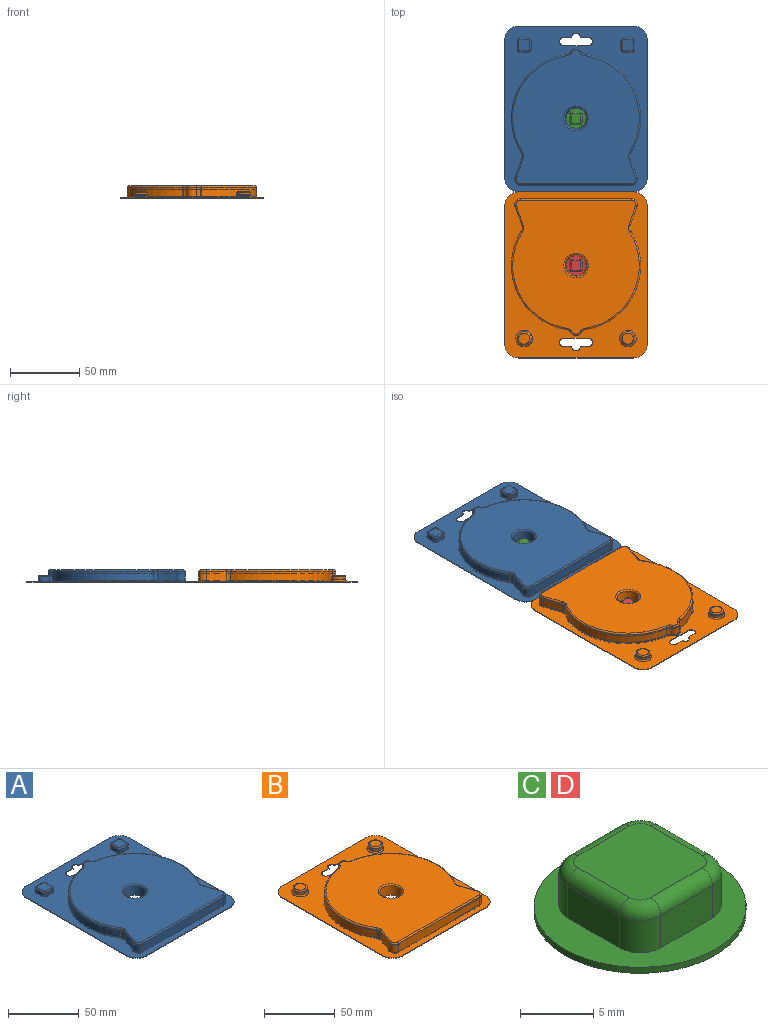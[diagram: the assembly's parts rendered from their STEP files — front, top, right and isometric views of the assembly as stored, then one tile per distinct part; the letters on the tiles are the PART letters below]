
ASSEMBLY  parts=4 mates=6
PART A: 168 faces, bbox 104.4x120x8.7 mm
  f0: plane 120x103mm, normal (0,0,-1), area 4033mm2, adj f3,f4,f5,f6,f7,f8,f9,f10
  f1: plane 15x15mm, normal (0,0,-1), area 12.1mm2, adj f48,f117
  f2: plane 120x103mm, normal (0,0,1), area 4313.1mm2, adj f3,f4,f5,f6,f7,f8,f9,f10
  f3: plane 100x0.5mm, normal (1,0,0), area 50mm2, adj f0,f2,f4,f16
  f4: cylinder r=10mm len=10mm, axis (0,0,-1), area 7.9mm2, adj f0,f2,f3,f5
  f5: plane 83x0.5mm, normal (0,1,0), area 41.5mm2, adj f0,f2,f4,f6
  f6: cylinder r=10mm len=10mm, axis (0,0,-1), area 7.9mm2, adj f0,f2,f5,f7
  f7: plane 100x0.5mm, normal (-1,0,0), area 50mm2, adj f0,f2,f6,f8
  f8: cylinder r=10mm len=10mm, axis (0,0,-1), area 7.9mm2, adj f0,f2,f7,f9
  f9: plane 83x0.5mm, normal (0,-1,0), area 41.5mm2, adj f0,f2,f8,f16
  f10: plane 18x0.5mm, normal (0,1,0), area 9mm2, adj f0,f2,f11,f15
  f11: cylinder r=3mm len=6mm, axis (0,0,-1), area 4.7mm2, adj f0,f2,f10,f12
  f12: plane 6x0.5mm, normal (0,-1,0), area 3mm2, adj f0,f2,f11,f13
  f13: cylinder r=3mm len=6mm, axis (0,0,-1), area 4.7mm2, adj f0,f2,f12,f14
  f14: plane 6x0.5mm, normal (0,-1,0), area 3mm2, adj f0,f2,f13,f15
  f15: cylinder r=3mm len=6mm, axis (0,0,-1), area 4.7mm2, adj f0,f2,f10,f14
  f16: cylinder r=10mm len=10mm, axis (0,0,-1), area 7.9mm2, adj f0,f2,f3,f9
  f17: cylinder r=4mm len=7.2mm, axis (0,0,-1), area 26.2mm2, adj f2,f18,f28,f58
  f18: plane 14.27x7.2mm, normal (-0.94,0.34,0), area 109mm2, adj f2,f17,f19,f60
  f19: cylinder r=4mm len=7.2mm, axis (0,0,-1), area 55.1mm2, adj f2,f18,f20,f59
  f20: plane 80.66x7.2mm, normal (0,-1,0), area 580.7mm2, adj f2,f19,f21,f57
  f21: cylinder r=4mm len=7.2mm, axis (0,0,-1), area 55.1mm2, adj f2,f20,f22,f55
  f22: plane 14.27x7.2mm, normal (0.94,0.34,0), area 109mm2, adj f2,f21,f23,f53
  f23: cylinder r=4mm len=7.2mm, axis (0,0,-1), area 26.2mm2, adj f2,f22,f24,f51
  f24: cylinder r=46.75mm len=71.42mm, axis (0,0,-1), area 672mm2, adj f2,f23,f25,f49
  f25: cylinder r=4mm len=7.2mm, axis (0,0,-1), area 28.2mm2, adj f2,f24,f26,f50
  f26: cylinder r=4mm len=7.2mm, axis (0,0,-1), area 64.5mm2, adj f2,f25,f27,f52
  f27: cylinder r=4mm len=7.2mm, axis (0,0,-1), area 28.2mm2, adj f2,f26,f28,f54
  f28: cylinder r=46.75mm len=71.42mm, axis (0,0,-1), area 672mm2, adj f2,f17,f27,f56
  f29: plane 97x91.5mm, normal (0,0,1), area 7034mm2, adj f49,f50,f51,f52,f53,f54,f55,f56
  f30: plane 6x3.2mm, normal (-1,0,0), area 19.2mm2, adj f2,f31,f37,f75
  f31: cylinder r=2mm len=3.2mm, axis (0,0,-1), area 10.1mm2, adj f2,f30,f32,f77
  f32: plane 6x3.2mm, normal (0,-1,0), area 19.2mm2, adj f2,f31,f33,f76
  f33: cylinder r=2mm len=3.2mm, axis (0,0,-1), area 10.1mm2, adj f2,f32,f34,f74
  f34: plane 6x3.2mm, normal (1,0,0), area 19.2mm2, adj f2,f33,f35,f72
  f35: cylinder r=2mm len=3.2mm, axis (0,0,-1), area 10.1mm2, adj f2,f34,f36,f70
  f36: plane 6x3.2mm, normal (0,1,0), area 19.2mm2, adj f2,f35,f37,f71
  f37: cylinder r=2mm len=3.2mm, axis (0,0,-1), area 10.1mm2, adj f2,f30,f36,f73
  f38: plane 8x8mm, normal (0,0,1), area 63.1mm2, adj f70,f71,f72,f73,f74,f75,f76,f77
  f39: plane 6x3.2mm, normal (1,0,0), area 19.2mm2, adj f2,f40,f46,f66
  f40: cylinder r=2mm len=3.2mm, axis (0,0,-1), area 10.1mm2, adj f2,f39,f41,f64
  f41: plane 6x3.2mm, normal (0,1,0), area 19.2mm2, adj f2,f40,f42,f62
  f42: cylinder r=2mm len=3.2mm, axis (0,0,-1), area 10.1mm2, adj f2,f41,f43,f63
  f43: plane 6x3.2mm, normal (-1,0,0), area 19.2mm2, adj f2,f42,f44,f65
  f44: cylinder r=2mm len=3.2mm, axis (0,0,-1), area 10.1mm2, adj f2,f43,f45,f67
  f45: plane 6x3.2mm, normal (0,-1,0), area 19.2mm2, adj f2,f44,f46,f69
  f46: cylinder r=2mm len=3.2mm, axis (0,0,-1), area 10.1mm2, adj f2,f39,f45,f68
  f47: plane 8x8mm, normal (0,0,1), area 63.1mm2, adj f62,f63,f64,f65,f66,f67,f68,f69
  f48: cone r=8mm half-angle=5deg, axis (0,0,1), area 372.3mm2, adj f1,f61
  f49: torus R=45.75mm, axis (0,0,1), area 145.5mm2, adj f24,f29,f50,f51
  f50: torus R=5mm, axis (0,0,1), area 6.7mm2, adj f25,f29,f49,f52
  f51: torus R=5mm, axis (0,0,1), area 6.2mm2, adj f23,f29,f49,f53
  f52: torus R=3mm, axis (0,0,1), area 12.8mm2, adj f26,f29,f50,f54
  f53: cylinder r=1mm len=14.6mm, axis (0.34,-0.94,0), area 23.8mm2, adj f22,f29,f51,f55
  f54: torus R=5mm, axis (0,0,1), area 6.7mm2, adj f27,f29,f52,f56
  f55: torus R=3mm, axis (0,0,1), area 10.9mm2, adj f21,f29,f53,f57
  f56: torus R=45.75mm, axis (0,0,1), area 145.5mm2, adj f28,f29,f54,f58
  f57: cylinder r=1mm len=80.66mm, axis (-1,0,0), area 126.7mm2, adj f20,f29,f55,f59
  f58: torus R=5mm, axis (0,0,1), area 6.2mm2, adj f17,f29,f56,f60
  f59: torus R=3mm, axis (0,0,1), area 10.9mm2, adj f19,f29,f57,f60
  f60: cylinder r=1mm len=14.6mm, axis (0.34,0.94,0), area 23.8mm2, adj f18,f29,f58,f59
  f61: torus R=8.92mm, axis (0,0,1), area 77.4mm2, adj f29,f48
  f62: cylinder r=1mm len=6mm, axis (1,0,0), area 9.4mm2, adj f41,f47,f63,f64
  f63: torus R=1mm, axis (0,0,1), area 4mm2, adj f42,f47,f62,f65
  f64: torus R=1mm, axis (0,0,1), area 4mm2, adj f40,f47,f62,f66
  f65: cylinder r=1mm len=6mm, axis (0,1,0), area 9.4mm2, adj f43,f47,f63,f67
  f66: cylinder r=1mm len=6mm, axis (0,-1,0), area 9.4mm2, adj f39,f47,f64,f68
  f67: torus R=1mm, axis (0,0,1), area 4mm2, adj f44,f47,f65,f69
  f68: torus R=1mm, axis (0,0,1), area 4mm2, adj f46,f47,f66,f69
  f69: cylinder r=1mm len=6mm, axis (-1,0,0), area 9.4mm2, adj f45,f47,f67,f68
  f70: torus R=1mm, axis (0,0,1), area 4mm2, adj f35,f38,f71,f72
  f71: cylinder r=1mm len=6mm, axis (1,0,0), area 9.4mm2, adj f36,f38,f70,f73
  f72: cylinder r=1mm len=6mm, axis (0,-1,0), area 9.4mm2, adj f34,f38,f70,f74
  f73: torus R=1mm, axis (0,0,1), area 4mm2, adj f37,f38,f71,f75
  f74: torus R=1mm, axis (0,0,1), area 4mm2, adj f33,f38,f72,f76
  f75: cylinder r=1mm len=6mm, axis (0,1,0), area 9.4mm2, adj f30,f38,f73,f77
  f76: cylinder r=1mm len=6mm, axis (-1,0,0), area 9.4mm2, adj f32,f38,f74,f77
  f77: torus R=1mm, axis (0,0,1), area 4mm2, adj f31,f38,f75,f76
  f78: cylinder r=4mm len=5.5mm, axis (0,0,-1), area 20.6mm2, adj f79,f89,f93,f114
  f79: plane 13.64x5.5mm, normal (-0.94,-0.35,0), area 80.2mm2, adj f78,f80,f95,f112
  f80: cylinder r=4mm len=5.5mm, axis (0,0,-1), area 42.5mm2, adj f79,f81,f97,f110
  f81: plane 80x5.5mm, normal (0,1,0), area 440mm2, adj f80,f82,f99,f108
  f82: cylinder r=4mm len=5.5mm, axis (0,0,-1), area 42.5mm2, adj f81,f83,f101,f106
  f83: plane 13.64x5.5mm, normal (0.94,-0.35,0), area 80.2mm2, adj f82,f84,f103,f104
  f84: cylinder r=4mm len=5.5mm, axis (0,0,-1), area 20.6mm2, adj f83,f85,f102,f105
  f85: cylinder r=46.5mm len=71.39mm, axis (0,0,-1), area 513.3mm2, adj f84,f86,f100,f107
  f86: cylinder r=4mm len=5.5mm, axis (0,0,-1), area 20.7mm2, adj f85,f87,f98,f109
  f87: cylinder r=4mm len=7.07mm, axis (0,0,-1), area 47.6mm2, adj f86,f88,f96,f111
  f88: cylinder r=4mm len=5.5mm, axis (0,0,-1), area 20.7mm2, adj f87,f89,f94,f113
  f89: cylinder r=46.5mm len=71.39mm, axis (0,0,-1), area 513.3mm2, adj f78,f88,f92,f115
  f90: cylinder r=8.5mm len=17mm, axis (0,0,-1), area 293.7mm2, adj f116,f117
  f91: plane 96.25x91mm, normal (0,0,-1), area 6910.7mm2, adj f104,f105,f106,f107,f108,f109,f110,f111
  f92: torus R=47.5mm, axis (0,0,1), area 147.7mm2, adj f0,f89,f93,f94
  f93: torus R=3mm, axis (0,0,1), area 5.4mm2, adj f0,f78,f92,f95
  f94: torus R=3mm, axis (0,0,1), area 5.4mm2, adj f0,f88,f92,f96
  f95: cylinder r=1mm len=14mm, axis (0.35,-0.94,0), area 22.9mm2, adj f0,f79,f93,f97
  f96: torus R=5mm, axis (0,0,1), area 14.8mm2, adj f0,f87,f94,f98
  f97: torus R=5mm, axis (0,0,1), area 13.2mm2, adj f0,f80,f95,f99
  f98: torus R=3mm, axis (0,0,1), area 5.4mm2, adj f0,f86,f96,f100
  f99: cylinder r=1mm len=80mm, axis (-1,0,0), area 125.7mm2, adj f0,f81,f97,f101
  f100: torus R=47.5mm, axis (0,0,1), area 147.7mm2, adj f0,f85,f98,f102
  f101: torus R=5mm, axis (0,0,1), area 13.2mm2, adj f0,f82,f99,f103
  f102: torus R=3mm, axis (0,0,1), area 5.4mm2, adj f0,f84,f100,f103
  f103: cylinder r=1mm len=14mm, axis (0.35,0.94,0), area 22.9mm2, adj f0,f83,f101,f102
  f104: cylinder r=1mm len=14mm, axis (0.35,0.94,0), area 22.9mm2, adj f83,f91,f105,f106
  f105: torus R=5mm, axis (0,0,-1), area 6.4mm2, adj f84,f91,f104,f107
  f106: torus R=3mm, axis (0,0,-1), area 11mm2, adj f82,f91,f104,f108
  f107: torus R=45.5mm, axis (0,0,-1), area 145.5mm2, adj f85,f91,f105,f109
  f108: cylinder r=1mm len=80mm, axis (-1,0,0), area 125.7mm2, adj f81,f91,f106,f110
  f109: torus R=5mm, axis (0,0,-1), area 6.5mm2, adj f86,f91,f107,f111
  f110: torus R=3mm, axis (0,0,-1), area 11mm2, adj f80,f91,f108,f112
  f111: torus R=3mm, axis (0,0,-1), area 12.4mm2, adj f87,f91,f109,f113
  f112: cylinder r=1mm len=14mm, axis (0.35,-0.94,0), area 22.9mm2, adj f79,f91,f110,f114
  f113: torus R=5mm, axis (0,0,-1), area 6.5mm2, adj f88,f91,f111,f115
  f114: torus R=5mm, axis (0,0,-1), area 6.4mm2, adj f78,f91,f112,f115
  f115: torus R=45.5mm, axis (0,0,-1), area 145.5mm2, adj f89,f91,f113,f114
  f116: torus R=9.5mm, axis (0,0,-1), area 87.5mm2, adj f90,f91
  f117: torus R=7.5mm, axis (0,0,1), area 80.3mm2, adj f1,f90
  f118: plane 5x1.7mm, normal (-1,0,0), area 8.5mm2, adj f119,f125,f143,f156
  f119: cylinder r=2mm len=2mm, axis (0,0,-1), area 5.3mm2, adj f118,f120,f141,f154
  f120: plane 5x1.7mm, normal (0,1,0), area 8.5mm2, adj f119,f121,f139,f152
  f121: cylinder r=2mm len=2mm, axis (0,0,-1), area 5.3mm2, adj f120,f122,f137,f153
  f122: plane 5x1.7mm, normal (1,0,0), area 8.5mm2, adj f121,f123,f136,f155
  f123: cylinder r=2mm len=2mm, axis (0,0,-1), area 5.3mm2, adj f122,f124,f138,f157
  f124: plane 5x1.7mm, normal (0,-1,0), area 8.5mm2, adj f123,f125,f140,f159
  f125: cylinder r=2mm len=2mm, axis (0,0,-1), area 5.3mm2, adj f118,f124,f142,f158
  f126: plane 7x7mm, normal (0,0,-1), area 48.1mm2, adj f152,f153,f154,f155,f156,f157,f158,f159
  f127: plane 5x1.7mm, normal (1,0,0), area 8.5mm2, adj f128,f134,f144,f165
  f128: cylinder r=2mm len=2mm, axis (0,0,-1), area 5.3mm2, adj f127,f129,f146,f167
  f129: plane 5x1.7mm, normal (0,-1,0), area 8.5mm2, adj f128,f130,f148,f166
  f130: cylinder r=2mm len=2mm, axis (0,0,-1), area 5.3mm2, adj f129,f131,f150,f164
  f131: plane 5x1.7mm, normal (-1,0,0), area 8.5mm2, adj f130,f132,f151,f162
  f132: cylinder r=2mm len=2mm, axis (0,0,-1), area 5.3mm2, adj f131,f133,f149,f160
  f133: plane 5x1.7mm, normal (0,1,0), area 8.5mm2, adj f132,f134,f147,f161
  f134: cylinder r=2mm len=2mm, axis (0,0,-1), area 5.3mm2, adj f127,f133,f145,f163
  f135: plane 7x7mm, normal (0,0,-1), area 48.1mm2, adj f160,f161,f162,f163,f164,f165,f166,f167
  f136: cylinder r=1mm len=5mm, axis (0,1,0), area 7.9mm2, adj f0,f122,f137,f138
  f137: torus R=3mm, axis (0,0,1), area 5.8mm2, adj f0,f121,f136,f139
  f138: torus R=3mm, axis (0,0,1), area 5.8mm2, adj f0,f123,f136,f140
  f139: cylinder r=1mm len=5mm, axis (-1,0,0), area 7.9mm2, adj f0,f120,f137,f141
  f140: cylinder r=1mm len=5mm, axis (1,0,0), area 7.9mm2, adj f0,f124,f138,f142
  f141: torus R=3mm, axis (0,0,1), area 5.8mm2, adj f0,f119,f139,f143
  f142: torus R=3mm, axis (0,0,1), area 5.8mm2, adj f0,f125,f140,f143
  f143: cylinder r=1mm len=5mm, axis (0,-1,0), area 7.9mm2, adj f0,f118,f141,f142
  f144: cylinder r=1mm len=5mm, axis (0,1,0), area 7.9mm2, adj f0,f127,f145,f146
  f145: torus R=3mm, axis (0,0,1), area 5.8mm2, adj f0,f134,f144,f147
  f146: torus R=3mm, axis (0,0,1), area 5.8mm2, adj f0,f128,f144,f148
  f147: cylinder r=1mm len=5mm, axis (-1,0,0), area 7.9mm2, adj f0,f133,f145,f149
  f148: cylinder r=1mm len=5mm, axis (1,0,0), area 7.9mm2, adj f0,f129,f146,f150
  f149: torus R=3mm, axis (0,0,1), area 5.8mm2, adj f0,f132,f147,f151
  f150: torus R=3mm, axis (0,0,1), area 5.8mm2, adj f0,f130,f148,f151
  f151: cylinder r=1mm len=5mm, axis (0,-1,0), area 7.9mm2, adj f0,f131,f149,f150
  f152: cylinder r=1mm len=5mm, axis (-1,0,0), area 7.9mm2, adj f120,f126,f153,f154
  f153: torus R=1mm, axis (0,0,-1), area 4mm2, adj f121,f126,f152,f155
  f154: torus R=1mm, axis (0,0,-1), area 4mm2, adj f119,f126,f152,f156
  f155: cylinder r=1mm len=5mm, axis (0,1,0), area 7.9mm2, adj f122,f126,f153,f157
  f156: cylinder r=1mm len=5mm, axis (0,-1,0), area 7.9mm2, adj f118,f126,f154,f158
  f157: torus R=1mm, axis (0,0,-1), area 4mm2, adj f123,f126,f155,f159
  f158: torus R=1mm, axis (0,0,-1), area 4mm2, adj f125,f126,f156,f159
  f159: cylinder r=1mm len=5mm, axis (1,0,0), area 7.9mm2, adj f124,f126,f157,f158
  f160: torus R=1mm, axis (0,0,-1), area 4mm2, adj f132,f135,f161,f162
  f161: cylinder r=1mm len=5mm, axis (-1,0,0), area 7.9mm2, adj f133,f135,f160,f163
  f162: cylinder r=1mm len=5mm, axis (0,-1,0), area 7.9mm2, adj f131,f135,f160,f164
  f163: torus R=1mm, axis (0,0,-1), area 4mm2, adj f134,f135,f161,f165
  f164: torus R=1mm, axis (0,0,-1), area 4mm2, adj f130,f135,f162,f166
  f165: cylinder r=1mm len=5mm, axis (0,1,0), area 7.9mm2, adj f127,f135,f163,f167
  f166: cylinder r=1mm len=5mm, axis (1,0,0), area 7.9mm2, adj f129,f135,f164,f167
  f167: torus R=1mm, axis (0,0,-1), area 4mm2, adj f128,f135,f165,f166
PART B: 100 faces, bbox 104.4x120x8.7 mm
  f0: plane 120x103mm, normal (0,0,-1), area 4069.5mm2, adj f3,f4,f5,f6,f7,f8,f9,f10
  f1: plane 15x15mm, normal (0,0,-1), area 12.1mm2, adj f34,f87
  f2: plane 120x103mm, normal (0,0,1), area 4280mm2, adj f3,f4,f5,f6,f7,f8,f9,f10
  f3: plane 100x0.5mm, normal (1,0,0), area 50mm2, adj f0,f2,f4,f16
  f4: cylinder r=10mm len=10mm, axis (0,0,-1), area 7.9mm2, adj f0,f2,f3,f5
  f5: plane 83x0.5mm, normal (0,1,0), area 41.5mm2, adj f0,f2,f4,f6
  f6: cylinder r=10mm len=10mm, axis (0,0,-1), area 7.9mm2, adj f0,f2,f5,f7
  f7: plane 100x0.5mm, normal (-1,0,0), area 50mm2, adj f0,f2,f6,f8
  f8: cylinder r=10mm len=10mm, axis (0,0,-1), area 7.9mm2, adj f0,f2,f7,f9
  f9: plane 83x0.5mm, normal (0,-1,0), area 41.5mm2, adj f0,f2,f8,f16
  f10: plane 18x0.5mm, normal (0,1,0), area 9mm2, adj f0,f2,f11,f15
  f11: cylinder r=3mm len=6mm, axis (0,0,-1), area 4.7mm2, adj f0,f2,f10,f12
  f12: plane 6x0.5mm, normal (0,-1,0), area 3mm2, adj f0,f2,f11,f13
  f13: cylinder r=3mm len=6mm, axis (0,0,-1), area 4.7mm2, adj f0,f2,f12,f14
  f14: plane 6x0.5mm, normal (0,-1,0), area 3mm2, adj f0,f2,f13,f15
  f15: cylinder r=3mm len=6mm, axis (0,0,-1), area 4.7mm2, adj f0,f2,f10,f14
  f16: cylinder r=10mm len=10mm, axis (0,0,-1), area 7.9mm2, adj f0,f2,f3,f9
  f17: cylinder r=4mm len=7.2mm, axis (0,0,-1), area 26.2mm2, adj f2,f18,f28,f44
  f18: plane 14.27x7.2mm, normal (-0.94,0.34,0), area 109mm2, adj f2,f17,f19,f46
  f19: cylinder r=4mm len=7.2mm, axis (0,0,-1), area 55.1mm2, adj f2,f18,f20,f45
  f20: plane 80.66x7.2mm, normal (0,-1,0), area 580.7mm2, adj f2,f19,f21,f43
  f21: cylinder r=4mm len=7.2mm, axis (0,0,-1), area 55.1mm2, adj f2,f20,f22,f41
  f22: plane 14.27x7.2mm, normal (0.94,0.34,0), area 109mm2, adj f2,f21,f23,f39
  f23: cylinder r=4mm len=7.2mm, axis (0,0,-1), area 26.2mm2, adj f2,f22,f24,f37
  f24: cylinder r=46.75mm len=71.42mm, axis (0,0,-1), area 672mm2, adj f2,f23,f25,f35
  f25: cylinder r=4mm len=7.2mm, axis (0,0,-1), area 28.2mm2, adj f2,f24,f26,f36
  f26: cylinder r=4mm len=7.2mm, axis (0,0,-1), area 64.5mm2, adj f2,f25,f27,f38
  f27: cylinder r=4mm len=7.2mm, axis (0,0,-1), area 28.2mm2, adj f2,f26,f28,f40
  f28: cylinder r=46.75mm len=71.42mm, axis (0,0,-1), area 672mm2, adj f2,f17,f27,f42
  f29: plane 97x91.5mm, normal (0,0,1), area 7034mm2, adj f35,f36,f37,f38,f39,f40,f41,f42
  f30: cylinder r=5mm len=10mm, axis (0,0,-1), area 69.1mm2, adj f94,f95
  f31: plane 8x8mm, normal (0,0,1), area 50.3mm2, adj f95
  f32: cylinder r=5mm len=10mm, axis (0,0,-1), area 69.1mm2, adj f92,f93
  f33: plane 8x8mm, normal (0,0,1), area 50.3mm2, adj f93
  f34: cone r=8mm half-angle=5deg, axis (0,0,1), area 372.3mm2, adj f1,f47
  f35: torus R=45.75mm, axis (0,0,1), area 145.5mm2, adj f24,f29,f36,f37
  f36: torus R=5mm, axis (0,0,1), area 6.7mm2, adj f25,f29,f35,f38
  f37: torus R=5mm, axis (0,0,1), area 6.2mm2, adj f23,f29,f35,f39
  f38: torus R=3mm, axis (0,0,1), area 12.8mm2, adj f26,f29,f36,f40
  f39: cylinder r=1mm len=14.6mm, axis (0.34,-0.94,0), area 23.8mm2, adj f22,f29,f37,f41
  f40: torus R=5mm, axis (0,0,1), area 6.7mm2, adj f27,f29,f38,f42
  f41: torus R=3mm, axis (0,0,1), area 10.9mm2, adj f21,f29,f39,f43
  f42: torus R=45.75mm, axis (0,0,1), area 145.5mm2, adj f28,f29,f40,f44
  f43: cylinder r=1mm len=80.66mm, axis (-1,0,0), area 126.7mm2, adj f20,f29,f41,f45
  f44: torus R=5mm, axis (0,0,1), area 6.2mm2, adj f17,f29,f42,f46
  f45: torus R=3mm, axis (0,0,1), area 10.9mm2, adj f19,f29,f43,f46
  f46: cylinder r=1mm len=14.6mm, axis (0.34,0.94,0), area 23.8mm2, adj f18,f29,f44,f45
  f47: torus R=8.92mm, axis (0,0,1), area 77.4mm2, adj f29,f34
  f48: cylinder r=4mm len=5.5mm, axis (0,0,-1), area 20.6mm2, adj f49,f59,f63,f84
  f49: plane 13.64x5.5mm, normal (-0.94,-0.35,0), area 80.2mm2, adj f48,f50,f65,f82
  f50: cylinder r=4mm len=5.5mm, axis (0,0,-1), area 42.5mm2, adj f49,f51,f67,f80
  f51: plane 80x5.5mm, normal (0,1,0), area 440mm2, adj f50,f52,f69,f78
  f52: cylinder r=4mm len=5.5mm, axis (0,0,-1), area 42.5mm2, adj f51,f53,f71,f76
  f53: plane 13.64x5.5mm, normal (0.94,-0.35,0), area 80.2mm2, adj f52,f54,f73,f74
  f54: cylinder r=4mm len=5.5mm, axis (0,0,-1), area 20.6mm2, adj f53,f55,f72,f75
  f55: cylinder r=46.5mm len=71.39mm, axis (0,0,-1), area 513.3mm2, adj f54,f56,f70,f77
  f56: cylinder r=4mm len=5.5mm, axis (0,0,-1), area 20.7mm2, adj f55,f57,f68,f79
  f57: cylinder r=4mm len=7.07mm, axis (0,0,-1), area 47.6mm2, adj f56,f58,f66,f81
  f58: cylinder r=4mm len=5.5mm, axis (0,0,-1), area 20.7mm2, adj f57,f59,f64,f83
  f59: cylinder r=46.5mm len=71.39mm, axis (0,0,-1), area 513.3mm2, adj f48,f58,f62,f85
  f60: cylinder r=8.5mm len=17mm, axis (0,0,-1), area 293.7mm2, adj f86,f87
  f61: plane 96.25x91mm, normal (0,0,-1), area 6910.7mm2, adj f74,f75,f76,f77,f78,f79,f80,f81
  f62: torus R=47.5mm, axis (0,0,1), area 147.7mm2, adj f0,f59,f63,f64
  f63: torus R=3mm, axis (0,0,1), area 5.4mm2, adj f0,f48,f62,f65
  f64: torus R=3mm, axis (0,0,1), area 5.4mm2, adj f0,f58,f62,f66
  f65: cylinder r=1mm len=14mm, axis (0.35,-0.94,0), area 22.9mm2, adj f0,f49,f63,f67
  f66: torus R=5mm, axis (0,0,1), area 14.8mm2, adj f0,f57,f64,f68
  f67: torus R=5mm, axis (0,0,1), area 13.2mm2, adj f0,f50,f65,f69
  f68: torus R=3mm, axis (0,0,1), area 5.4mm2, adj f0,f56,f66,f70
  f69: cylinder r=1mm len=80mm, axis (-1,0,0), area 125.7mm2, adj f0,f51,f67,f71
  f70: torus R=47.5mm, axis (0,0,1), area 147.7mm2, adj f0,f55,f68,f72
  f71: torus R=5mm, axis (0,0,1), area 13.2mm2, adj f0,f52,f69,f73
  f72: torus R=3mm, axis (0,0,1), area 5.4mm2, adj f0,f54,f70,f73
  f73: cylinder r=1mm len=14mm, axis (0.35,0.94,0), area 22.9mm2, adj f0,f53,f71,f72
  f74: cylinder r=1mm len=14mm, axis (0.35,0.94,0), area 22.9mm2, adj f53,f61,f75,f76
  f75: torus R=5mm, axis (0,0,-1), area 6.4mm2, adj f54,f61,f74,f77
  f76: torus R=3mm, axis (0,0,-1), area 11mm2, adj f52,f61,f74,f78
  f77: torus R=45.5mm, axis (0,0,-1), area 145.5mm2, adj f55,f61,f75,f79
  f78: cylinder r=1mm len=80mm, axis (-1,0,0), area 125.7mm2, adj f51,f61,f76,f80
  f79: torus R=5mm, axis (0,0,-1), area 6.5mm2, adj f56,f61,f77,f81
  f80: torus R=3mm, axis (0,0,-1), area 11mm2, adj f50,f61,f78,f82
  f81: torus R=3mm, axis (0,0,-1), area 12.4mm2, adj f57,f61,f79,f83
  f82: cylinder r=1mm len=14mm, axis (0.35,-0.94,0), area 22.9mm2, adj f49,f61,f80,f84
  f83: torus R=5mm, axis (0,0,-1), area 6.5mm2, adj f58,f61,f81,f85
  f84: torus R=5mm, axis (0,0,-1), area 6.4mm2, adj f48,f61,f82,f85
  f85: torus R=45.5mm, axis (0,0,-1), area 145.5mm2, adj f59,f61,f83,f84
  f86: torus R=9.5mm, axis (0,0,-1), area 87.5mm2, adj f60,f61
  f87: torus R=7.5mm, axis (0,0,1), area 80.3mm2, adj f1,f60
  f88: cylinder r=4.5mm len=9mm, axis (0,0,-1), area 48.1mm2, adj f96,f97
  f89: plane 7x7mm, normal (0,0,-1), area 38.5mm2, adj f97
  f90: cylinder r=4.5mm len=9mm, axis (0,0,-1), area 48.1mm2, adj f98,f99
  f91: plane 7x7mm, normal (0,0,-1), area 38.5mm2, adj f99
  f92: torus R=6mm, axis (0,0,1), area 52.9mm2, adj f2,f32
  f93: torus R=4mm, axis (0,0,1), area 45.8mm2, adj f32,f33
  f94: torus R=6mm, axis (0,0,1), area 52.9mm2, adj f2,f30
  f95: torus R=4mm, axis (0,0,1), area 45.8mm2, adj f30,f31
  f96: torus R=5.5mm, axis (0,0,1), area 48mm2, adj f0,f88
  f97: torus R=3.5mm, axis (0,0,-1), area 40.8mm2, adj f88,f89
  f98: torus R=5.5mm, axis (0,0,1), area 48mm2, adj f0,f90
  f99: torus R=3.5mm, axis (0,0,-1), area 40.8mm2, adj f90,f91
PART C: 45 faces, bbox 14.5x14.5x4.2 mm
  f0: plane 14.48x14.48mm, normal (0,0,1), area 87.1mm2, adj f1,f3,f4,f5,f6,f7,f8,f9
  f1: cylinder r=7.24mm len=14.48mm, axis (0,0,-1), area 22.7mm2, adj f0,f2
  f2: plane 14.48x14.48mm, normal (0,0,-1), area 89mm2, adj f1,f29,f30,f31,f32,f33,f34,f35
  f3: plane 5x2.7mm, normal (1,0,0), area 13.5mm2, adj f0,f4,f10,f16
  f4: cylinder r=2mm len=2.7mm, axis (0,0,-1), area 8.5mm2, adj f0,f3,f5,f14
  f5: plane 5x2.7mm, normal (0,1,0), area 13.5mm2, adj f0,f4,f6,f12
  f6: cylinder r=2mm len=2.7mm, axis (0,0,-1), area 8.5mm2, adj f0,f5,f7,f13
  f7: plane 5x2.7mm, normal (-1,0,0), area 13.5mm2, adj f0,f6,f8,f15
  f8: cylinder r=2mm len=2.7mm, axis (0,0,-1), area 8.5mm2, adj f0,f7,f9,f17
  f9: plane 5x2.7mm, normal (0,-1,0), area 13.5mm2, adj f0,f8,f10,f19
  f10: cylinder r=2mm len=2.7mm, axis (0,0,-1), area 8.5mm2, adj f0,f3,f9,f18
  f11: plane 7x7mm, normal (0,0,1), area 48.1mm2, adj f12,f13,f14,f15,f16,f17,f18,f19
  f12: cylinder r=1mm len=5mm, axis (1,0,0), area 7.9mm2, adj f5,f11,f13,f14
  f13: torus R=1mm, axis (0,0,1), area 4mm2, adj f6,f11,f12,f15
  f14: torus R=1mm, axis (0,0,1), area 4mm2, adj f4,f11,f12,f16
  f15: cylinder r=1mm len=5mm, axis (0,1,0), area 7.9mm2, adj f7,f11,f13,f17
  f16: cylinder r=1mm len=5mm, axis (0,-1,0), area 7.9mm2, adj f3,f11,f14,f18
  f17: torus R=1mm, axis (0,0,1), area 4mm2, adj f8,f11,f15,f19
  f18: torus R=1mm, axis (0,0,1), area 4mm2, adj f10,f11,f16,f19
  f19: cylinder r=1mm len=5mm, axis (-1,0,0), area 7.9mm2, adj f9,f11,f17,f18
  f20: plane 4x2.2mm, normal (1,0,0), area 8.8mm2, adj f21,f27,f31,f40
  f21: cylinder r=2mm len=2.2mm, axis (0,0,-1), area 6.9mm2, adj f20,f22,f29,f38
  f22: plane 4x2.2mm, normal (0,-1,0), area 8.8mm2, adj f21,f23,f30,f37
  f23: cylinder r=2mm len=2.2mm, axis (0,0,-1), area 6.9mm2, adj f22,f24,f32,f39
  f24: plane 4x2.2mm, normal (-1,0,0), area 8.8mm2, adj f23,f25,f34,f41
  f25: cylinder r=2mm len=2.2mm, axis (0,0,-1), area 6.9mm2, adj f24,f26,f36,f43
  f26: plane 4x2.2mm, normal (0,1,0), area 8.8mm2, adj f25,f27,f35,f44
  f27: cylinder r=2mm len=2.2mm, axis (0,0,-1), area 6.9mm2, adj f20,f26,f33,f42
  f28: plane 7x7mm, normal (0,0,-1), area 47.1mm2, adj f37,f38,f39,f40,f41,f42,f43,f44
  f29: torus R=2.5mm, axis (0,0,-1), area 2.7mm2, adj f2,f21,f30,f31
  f30: cylinder r=0.5mm len=4mm, axis (-1,0,0), area 3.1mm2, adj f2,f22,f29,f32
  f31: cylinder r=0.5mm len=4mm, axis (0,-1,0), area 3.1mm2, adj f2,f20,f29,f33
  f32: torus R=2.5mm, axis (0,0,-1), area 2.7mm2, adj f2,f23,f30,f34
  f33: torus R=2.5mm, axis (0,0,-1), area 2.7mm2, adj f2,f27,f31,f35
  f34: cylinder r=0.5mm len=4mm, axis (0,1,0), area 3.1mm2, adj f2,f24,f32,f36
  f35: cylinder r=0.5mm len=4mm, axis (1,0,0), area 3.1mm2, adj f2,f26,f33,f36
  f36: torus R=2.5mm, axis (0,0,-1), area 2.7mm2, adj f2,f25,f34,f35
  f37: cylinder r=0.5mm len=4mm, axis (1,0,0), area 3.1mm2, adj f22,f28,f38,f39
  f38: torus R=1.5mm, axis (0,0,-1), area 2.2mm2, adj f21,f28,f37,f40
  f39: torus R=1.5mm, axis (0,0,-1), area 2.2mm2, adj f23,f28,f37,f41
  f40: cylinder r=0.5mm len=4mm, axis (0,1,0), area 3.1mm2, adj f20,f28,f38,f42
  f41: cylinder r=0.5mm len=4mm, axis (0,-1,0), area 3.1mm2, adj f24,f28,f39,f43
  f42: torus R=1.5mm, axis (0,0,-1), area 2.2mm2, adj f27,f28,f40,f44
  f43: torus R=1.5mm, axis (0,0,-1), area 2.2mm2, adj f25,f28,f41,f44
  f44: cylinder r=0.5mm len=4mm, axis (-1,0,0), area 3.1mm2, adj f26,f28,f42,f43
PART D: same geometry as C
PLACE A t=(0.95,103.89,64.15)mm
PLACE B rot(axis=(0,0,1),180deg) t=(103.95,103.89,64.15)mm
PLACE C rot(axis=(0,0,1),0deg) t=(0.95,103.89,64.15)mm
PLACE D rot(axis=(0,0,-1),0deg) t=(0.95,-2.61,64.15)mm
MATE cylindrical C.f1 <-> A.f24  axis (0,0,-1) through (52.45,157.14,64.4)mm
MATE planar B.f9 <-> A.f9  axis (0,1,0) through (52.45,103.89,64.4)mm
MATE planar D.f1 <-> B.f1  axis (0,0,-1) through (52.45,50.64,64.15)mm
MATE cylindrical D.f1 <-> B.f24  axis (0,0,1) through (52.45,50.64,64.65)mm
MATE planar C.f2 <-> B.f1  axis (0,0,-1) through (52.44,157.13,64.15)mm
MATE planar B.f3 <-> A.f7  axis (-1,0,0) through (0.95,43.89,64.4)mm
